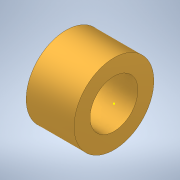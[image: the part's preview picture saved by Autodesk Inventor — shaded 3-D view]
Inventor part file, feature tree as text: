
AUTODESK INVENTOR PART (.ipt)
format: ipt  version: 2022 (Build 260153070, 153G)  size: 110,592 bytes
history: native  units: mm
features: sketch x3, extrude x2
ambient origin geometry x8: Origin, YZ Plane, XZ Plane, XY Plane, X Axis, Y Axis, Z Axis, Center Point
bodies: Solid1 (feature_tree)
feature tree (5):
  extrude  "Extrusion1"  Depth=6.0mm TaperAngle=0.0deg
  extrude  "Extrusion2"  TaperAngle=0.0deg  [1 undecoded]
  sketch  "Sketch3"
  sketch  "Sketch1"  dims[d0=10.0mm d1=6.0mm d2=0.0mm]
  sketch  "Sketch2"  dims[d3=6.0mm d4=0.0mm d5=0.0mm]
note: 1 required parameter value undecoded (feature->parameter linkage not recoverable at this tier; creation-order binding heuristic only, values carry confidence <= 0.55)
